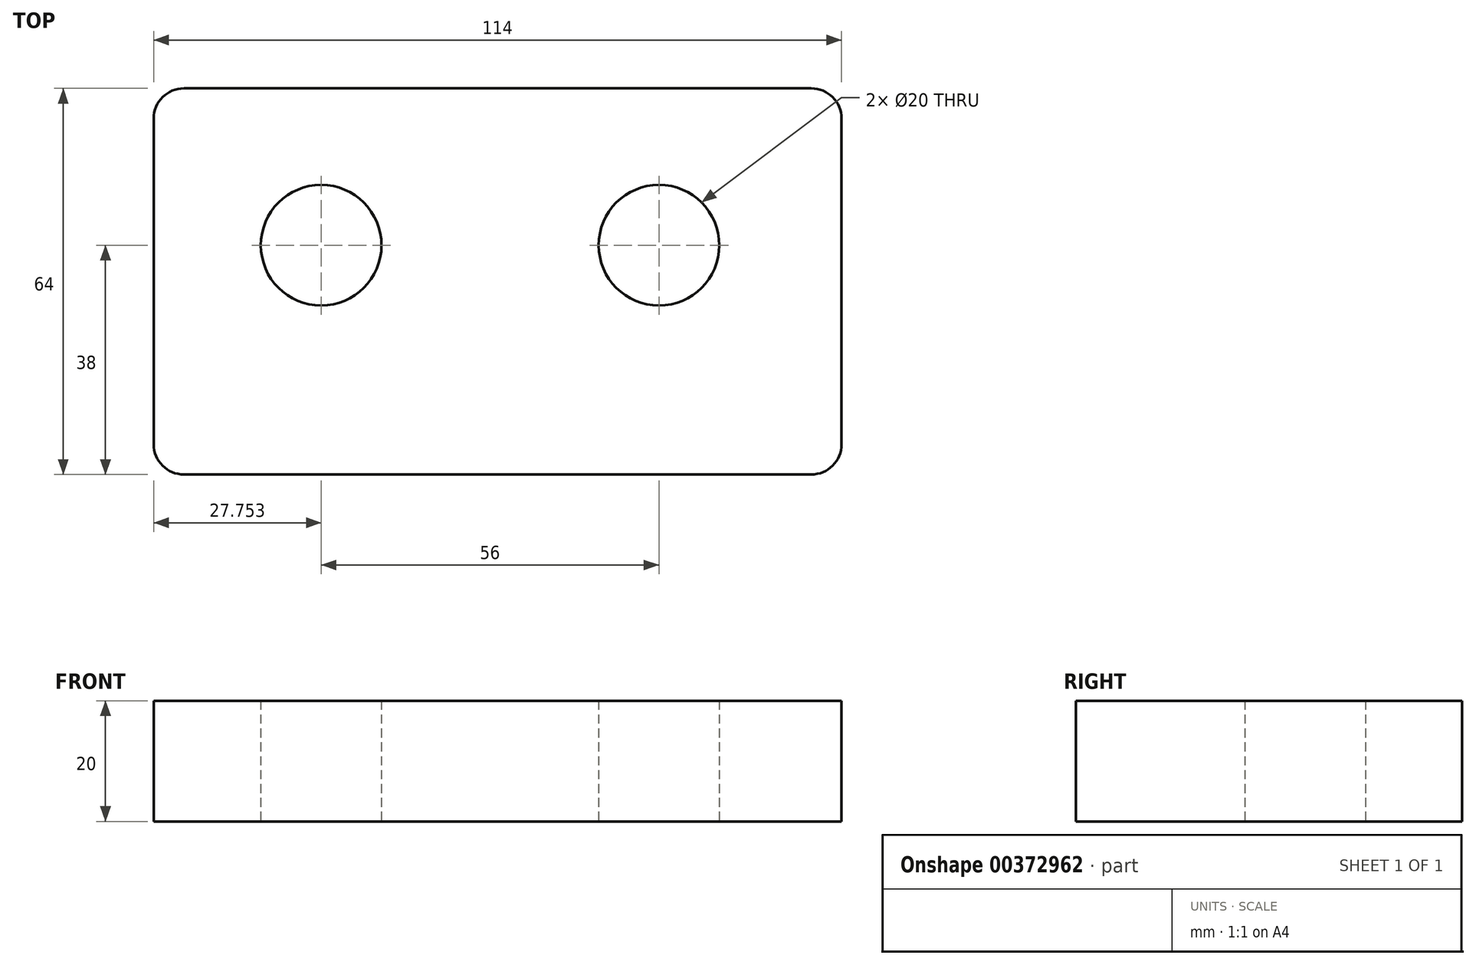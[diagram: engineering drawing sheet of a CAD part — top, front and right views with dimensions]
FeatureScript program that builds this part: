
annotation { "Feature Type Name" : "Feature", "Feature Type Description" : "" }
export const myFeature = defineFeature(function(context is Context, id is Id, definition is map)
    precondition{}
    {
        {
            var Q0;
            Q0=qCreatedBy(makeId("Top.planeOp"),FACE);
            var sketch = newSketch(context, id + "F0", { "sketchPlane" : qUnion([Q0])});
            skLineSegment(sketch, "E0.bottom", {"start": v(52, -38) * mm, "end": v(-52, -38) * mm});
            skLineSegment(sketch, "E0.left", {"start": v(57, -33) * mm, "end": v(57, 21) * mm});
            skLineSegment(sketch, "E0.right", {"start": v(-57, -33) * mm, "end": v(-57, 21) * mm});
            skPoint(sketch, "E0.middle", {"position": v(0, 0) * mm});
            skArc(sketch, "E1", {"start": v(-52, 26) * mm, "mid": v(-55.54, 24.54) * mm, "end": v(-57, 21) * mm});
            skArc(sketch, "E2", {"start": v(57, 21) * mm, "mid": v(55.54, 24.54) * mm, "end": v(52, 26) * mm});
            skArc(sketch, "E3", {"start": v(-57, -33) * mm, "mid": v(-55.54, -36.54) * mm, "end": v(-52, -38) * mm});
            skArc(sketch, "E4", {"start": v(52, -38) * mm, "mid": v(55.54, -36.54) * mm, "end": v(57, -33) * mm});
            skPoint(sketch, "E5.orphan", {"position": v(57, 38) * mm});
            skPoint(sketch, "E6.orphan", {"position": v(57, -38) * mm});
            skPoint(sketch, "E7.orphan", {"position": v(-57, -38) * mm});
            skPoint(sketch, "E8.orphan", {"position": v(-57, 38) * mm});
            skCircle(sketch, "E9", {"center": v(-29.25, 0) * mm, "radius": 10 * mm});
            skCircle(sketch, "E10", {"center": v(26.75, 0) * mm, "radius": 10 * mm});
            skLineSegment(sketch, "E11", {"start": v(52, 26) * mm, "end": v(-52, 26) * mm});
            skSolve(sketch);
        }
        {
            var Q0;
            Q0 = qSketchRegion(id + "F0", true);
            extrude(context, id + "F1", {"entities" : qUnion([Q0]), "depth" : 20 * mm});
        }
    });
